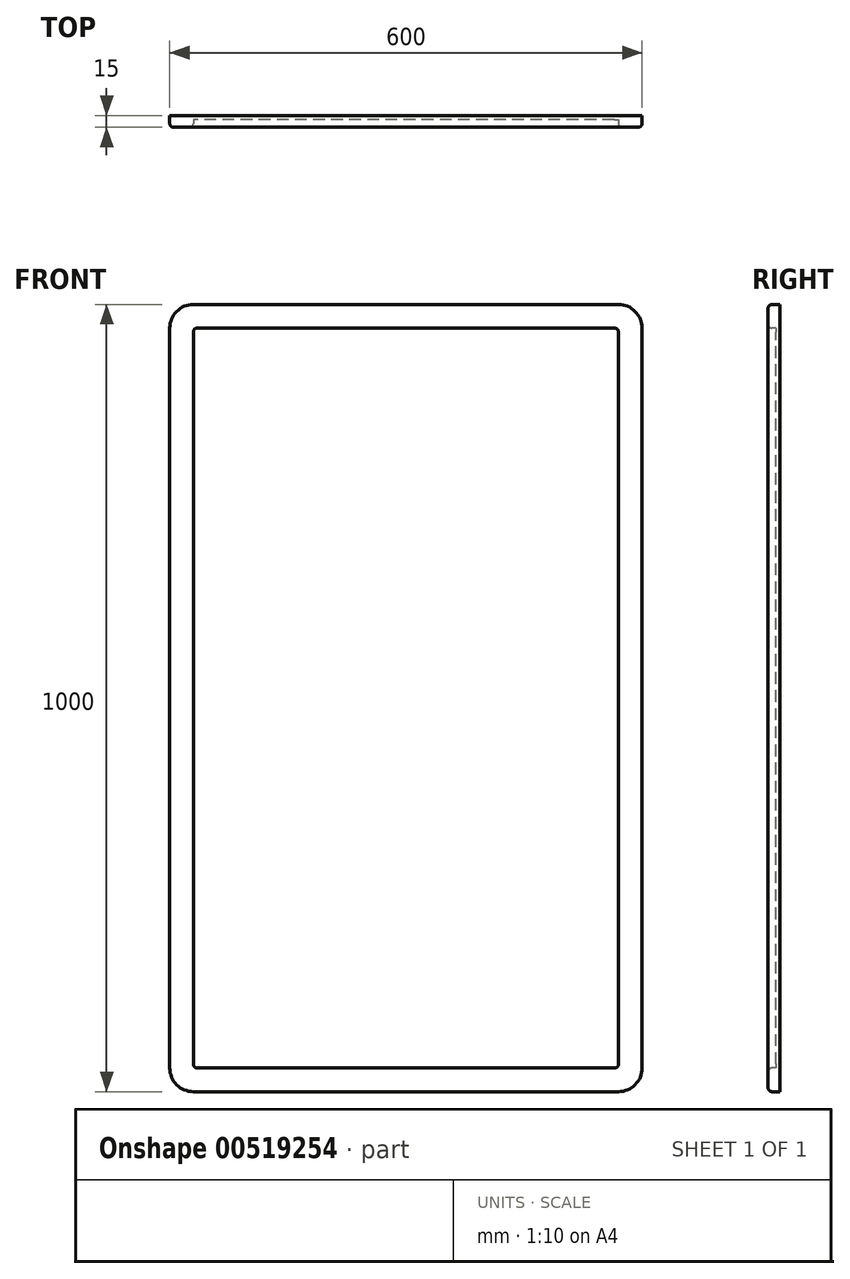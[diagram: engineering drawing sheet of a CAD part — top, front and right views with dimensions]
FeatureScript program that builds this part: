
annotation { "Feature Type Name" : "Feature", "Feature Type Description" : "" }
export const myFeature = defineFeature(function(context is Context, id is Id, definition is map)
    precondition{}
    {
        {
            var Q0;
            Q0=qCreatedBy(makeId("Front.planeOp"),FACE);
            var sketch = newSketch(context, id + "F0", { "sketchPlane" : qUnion([Q0])});
            skLineSegment(sketch, "E0.bottom", {"start": v(0, 0) * mm, "end": v(600, 0) * mm});
            skLineSegment(sketch, "E0.top", {"start": v(0, 1000) * mm, "end": v(600, 1000) * mm});
            skLineSegment(sketch, "E0.left", {"start": v(0, 0) * mm, "end": v(0, 1000) * mm});
            skLineSegment(sketch, "E0.right", {"start": v(600, 0) * mm, "end": v(600, 1000) * mm});
            skSolve(sketch);
        }
        {
            var Q0;
            Q0 = qSketchRegion(id + "F0", true);
            extrude(context, id + "F1", {"entities" : qUnion([Q0]), "depth" : 15 * mm, "offsetDistance" : 25 * mm});
        }
        {
            var Q0;
            Q0=makeQuery(id+"F1.opExtrude","CAP_FACE",FACE,{"disambiguationData":[OSD([sQuery(id+"F0.wireOp",EDGE,"E0.bottom"),sQuery(id+"F0.wireOp",EDGE,"E0.top"),sQuery(id+"F0.wireOp",EDGE,"E0.left"),sQuery(id+"F0.wireOp",EDGE,"E0.right")])],"isStart":false});
            var sketch = newSketch(context, id + "F2", { "sketchPlane" : qUnion([Q0])});
            skLineSegment(sketch, "E1.0", {"start": v(570, 970) * mm, "end": v(30, 970) * mm});
            skLineSegment(sketch, "E1.1", {"start": v(570, 30) * mm, "end": v(570, 970) * mm});
            skLineSegment(sketch, "E1.2", {"start": v(30, 30) * mm, "end": v(570, 30) * mm});
            skLineSegment(sketch, "E1.3", {"start": v(30, 970) * mm, "end": v(30, 30) * mm});
            skSolve(sketch);
        }
        {
            var Q0;
            Q0 = qSketchRegion(id + "F2", true);
            extrude(context, id + "F3", {"entities" : qUnion([Q0]), "operationType" : NewBodyOperationType.REMOVE, "oppositeDirection" : true, "depth" : 10 * mm, "offsetDistance" : 25 * mm});
        }
        {
            var Q0;
            Q0=makeQuery(id+"F1.opExtrude","SWEPT_EDGE",EDGE,{"disambiguationData":[OSD([sQuery(id+"F0.wireOp",EDGE,"E0.top"),sQuery(id+"F0.wireOp",EDGE,"E0.left")])]});
            var Q1;
            Q1=makeQuery(id+"F1.opExtrude","SWEPT_EDGE",EDGE,{"disambiguationData":[OSD([sQuery(id+"F0.wireOp",EDGE,"E0.top"),sQuery(id+"F0.wireOp",EDGE,"E0.right")])]});
            var Q2;
            Q2=makeQuery(id+"F1.opExtrude","SWEPT_EDGE",EDGE,{"disambiguationData":[OSD([sQuery(id+"F0.wireOp",EDGE,"E0.bottom"),sQuery(id+"F0.wireOp",EDGE,"E0.right")])]});
            var Q3;
            Q3=makeQuery(id+"F1.opExtrude","SWEPT_EDGE",EDGE,{"disambiguationData":[OSD([sQuery(id+"F0.wireOp",EDGE,"E0.bottom"),sQuery(id+"F0.wireOp",EDGE,"E0.left")])]});
            fillet(context, id + "F4", {"entities" : qUnion([Q0, Q1, Q2, Q3]), "radius" : 30 * mm, "tangentPropagation" : true, "allowEdgeOverflow" : false});
        }
        {
            var Q0;
            Q0=makeQuery(id+"F3.boolean.opBoolean","COPY",EDGE,{"derivedFrom":makeQuery(id+"F3.opExtrude","SWEPT_EDGE",EDGE,{"disambiguationData":[OSD([sQuery(id+"F2.wireOp",EDGE,"E1.2"),sQuery(id+"F2.wireOp",EDGE,"E1.3")])]})});
            var Q1;
            Q1=makeQuery(id+"F3.boolean.opBoolean","COPY",EDGE,{"derivedFrom":makeQuery(id+"F3.opExtrude","SWEPT_EDGE",EDGE,{"disambiguationData":[OSD([sQuery(id+"F2.wireOp",EDGE,"E1.1"),sQuery(id+"F2.wireOp",EDGE,"E1.2")])]})});
            var Q2;
            Q2=makeQuery(id+"F3.boolean.opBoolean","COPY",EDGE,{"derivedFrom":makeQuery(id+"F3.opExtrude","SWEPT_EDGE",EDGE,{"disambiguationData":[OSD([sQuery(id+"F2.wireOp",EDGE,"E1.0"),sQuery(id+"F2.wireOp",EDGE,"E1.1")])]})});
            var Q3;
            Q3=makeQuery(id+"F3.boolean.opBoolean","COPY",EDGE,{"derivedFrom":makeQuery(id+"F3.opExtrude","SWEPT_EDGE",EDGE,{"disambiguationData":[OSD([sQuery(id+"F2.wireOp",EDGE,"E1.0"),sQuery(id+"F2.wireOp",EDGE,"E1.3")])]})});
            fillet(context, id + "F5", {"entities" : qUnion([Q0, Q1, Q2, Q3]), "radius" : 5 * mm, "tangentPropagation" : true, "allowEdgeOverflow" : false});
        }
        {
            var Q0;
            Q0=makeQuery(id+"F1.opExtrude","CAP_FACE",FACE,{"disambiguationData":[OSD([sQuery(id+"F0.wireOp",EDGE,"E0.bottom"),sQuery(id+"F0.wireOp",EDGE,"E0.top"),sQuery(id+"F0.wireOp",EDGE,"E0.left"),sQuery(id+"F0.wireOp",EDGE,"E0.right")])],"isStart":false});
            fillet(context, id + "F6", {"entities" : qUnion([Q0]), "radius" : 5 * mm, "tangentPropagation" : true, "allowEdgeOverflow" : false});
        }
    });
